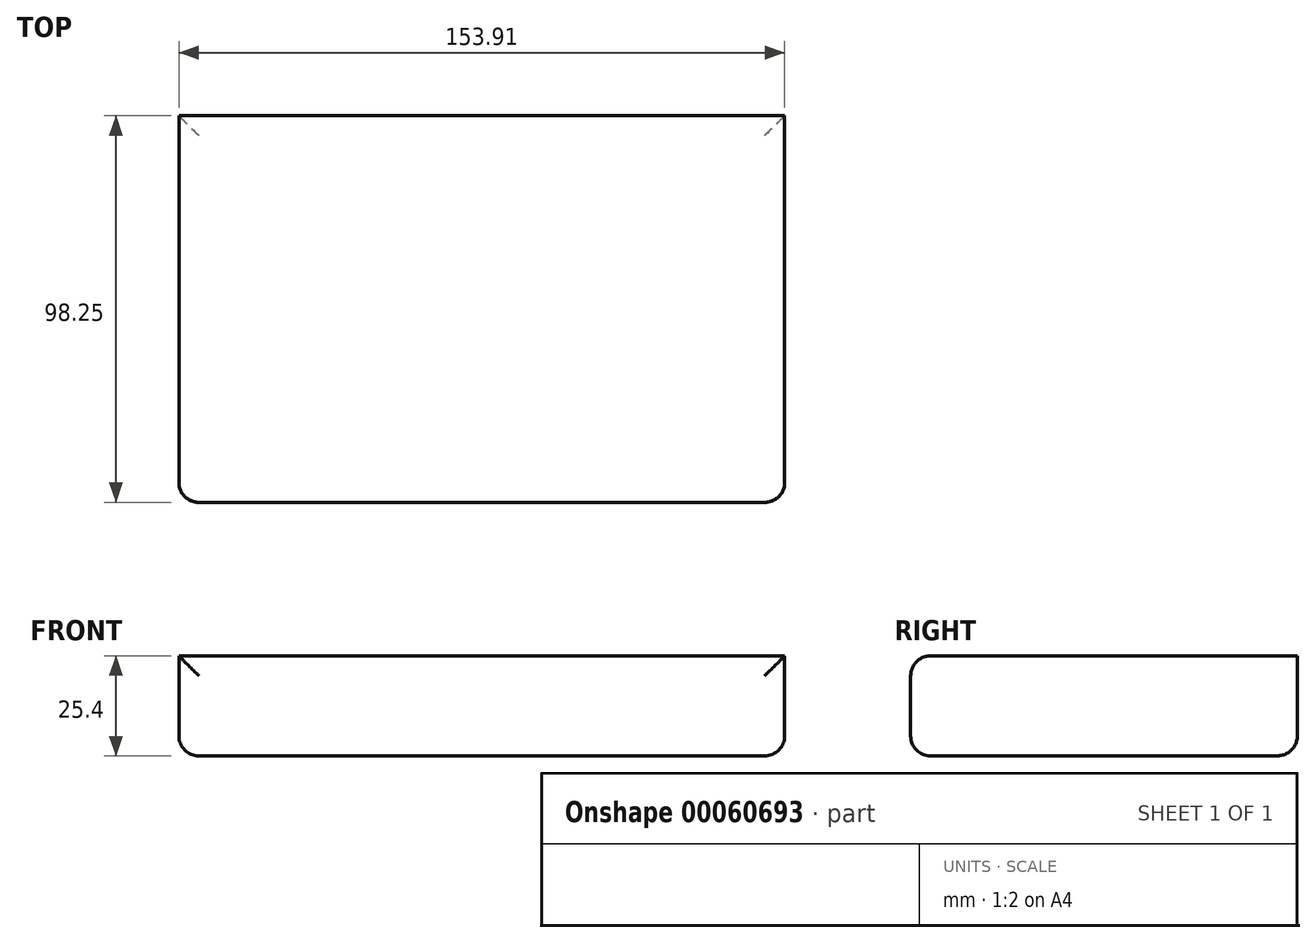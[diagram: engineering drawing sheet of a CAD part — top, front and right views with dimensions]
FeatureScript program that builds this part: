
annotation { "Feature Type Name" : "Feature", "Feature Type Description" : "" }
export const myFeature = defineFeature(function(context is Context, id is Id, definition is map)
    precondition{}
    {
        {
            var Q0;
            Q0=qCreatedBy(makeId("Top.planeOp"),FACE);
            var sketch = newSketch(context, id + "F0", { "sketchPlane" : qUnion([Q0])});
            skLineSegment(sketch, "E0.bottom", {"start": v(-94.05, 36.12) * mm, "end": v(59.86, 36.12) * mm});
            skLineSegment(sketch, "E0.top", {"start": v(-94.05, -62.13) * mm, "end": v(59.86, -62.13) * mm});
            skLineSegment(sketch, "E0.left", {"start": v(-94.05, 36.12) * mm, "end": v(-94.05, -62.13) * mm});
            skLineSegment(sketch, "E0.right", {"start": v(59.86, 36.12) * mm, "end": v(59.86, -62.13) * mm});
            skSolve(sketch);
        }
        {
            var Q0;
            Q0=makeQuery(id+"F0.imprint","IMPRINT",FACE,{"disambiguationData":[TD([[makeQuery(id+"F0.imprint","IMPRINT",EDGE,{"derivedFrom":sQuery(id+"F0.wireOp",EDGE,"E0.bottom")}),-1.0]])]});
            extrude(context, id + "F1", {"entities" : qUnion([Q0]), "depth" : 25.4 * mm});
        }
        {
            var Q0;
            Q0=makeQuery(id+"F1.opExtrude","SWEPT_FACE",FACE,{"disambiguationData":[OSD([sQuery(id+"F0.wireOp",EDGE,"E0.top")])]});
            var Q1;
            Q1=makeQuery(id+"F1.opExtrude","CAP_FACE",FACE,{"disambiguationData":[OSD([sQuery(id+"F0.wireOp",EDGE,"E0.bottom"),sQuery(id+"F0.wireOp",EDGE,"E0.top"),sQuery(id+"F0.wireOp",EDGE,"E0.left"),sQuery(id+"F0.wireOp",EDGE,"E0.right")])],"isStart":true});
            fillet(context, id + "F2", {"entities" : qUnion([Q0, Q1]), "radius" : 5.08 * mm, "tangentPropagation" : true, "allowEdgeOverflow" : false});
        }
    });
